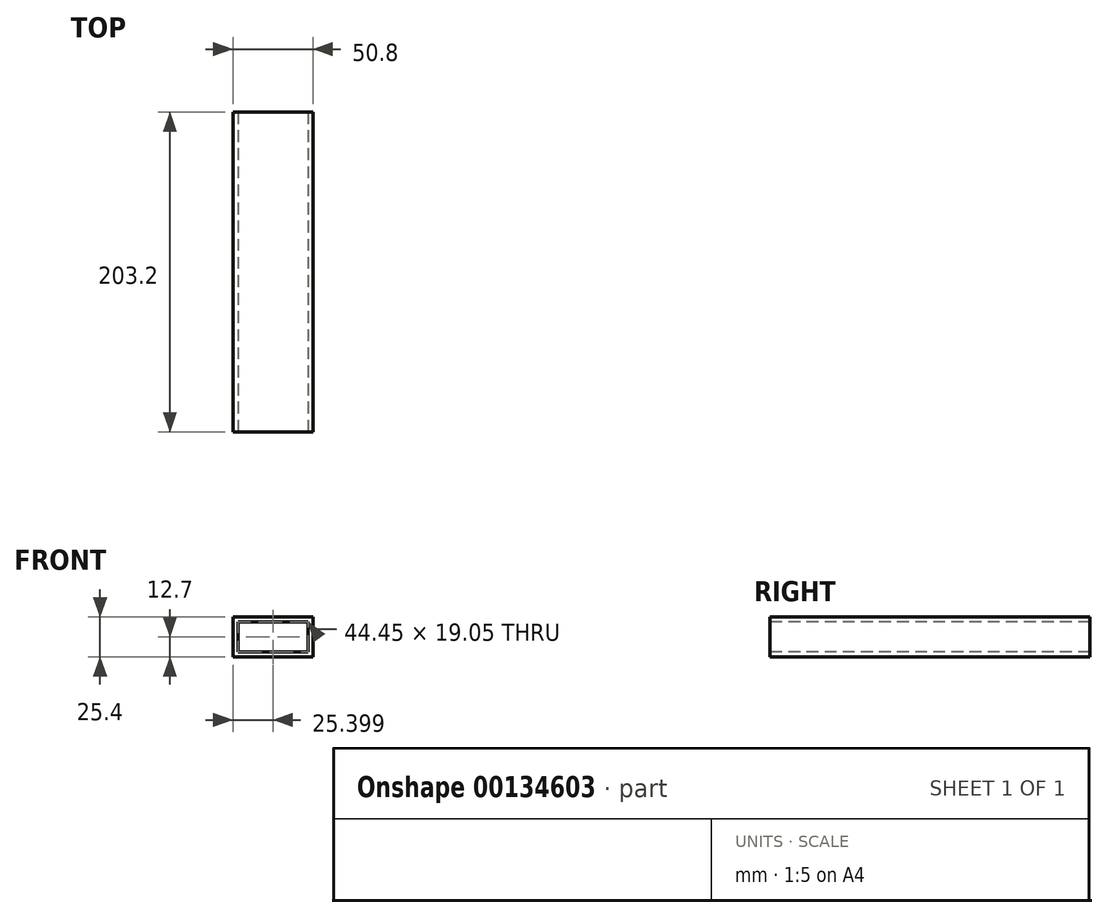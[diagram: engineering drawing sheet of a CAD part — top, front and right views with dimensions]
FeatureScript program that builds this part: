
annotation { "Feature Type Name" : "Feature", "Feature Type Description" : "" }
export const myFeature = defineFeature(function(context is Context, id is Id, definition is map)
    precondition{}
    {
        {
            var Q0;
            Q0=qCreatedBy(makeId("Top.planeOp"),FACE);
            var sketch = newSketch(context, id + "F0", { "sketchPlane" : qUnion([Q0])});
            skLineSegment(sketch, "E0.bottom", {"start": v(-36.05, 90.68) * mm, "end": v(14.75, 90.68) * mm});
            skLineSegment(sketch, "E0.top", {"start": v(-36.05, -112.52) * mm, "end": v(14.75, -112.52) * mm});
            skLineSegment(sketch, "E0.left", {"start": v(-36.05, 90.68) * mm, "end": v(-36.05, -112.52) * mm});
            skLineSegment(sketch, "E0.right", {"start": v(14.75, 90.68) * mm, "end": v(14.75, -112.52) * mm});
            skSolve(sketch);
        }
        {
            var Q0;
            Q0 = qSketchRegion(id + "F0", true);
            extrude(context, id + "F1", {"entities" : qUnion([Q0]), "endBound" : BoundingType.SYMMETRIC, "depth" : 25.4 * mm});
        }
        {
            var Q0;
            Q0=makeQuery(id+"F1.opExtrude","SWEPT_FACE",FACE,{"disambiguationData":[OSD([sQuery(id+"F0.wireOp",EDGE,"E0.top")])]});
            var Q1;
            Q1=makeQuery(id+"F1.opExtrude","SWEPT_FACE",FACE,{"disambiguationData":[OSD([sQuery(id+"F0.wireOp",EDGE,"E0.bottom")])]});
            var Q2;
            Q2=makeQuery(id+"F1.opExtrude","SWEPT_BODY",BODY,{"disambiguationData":[OSD([sQuery(id+"F0.wireOp",EDGE,"E0.bottom"),sQuery(id+"F0.wireOp",EDGE,"E0.top"),sQuery(id+"F0.wireOp",EDGE,"E0.left"),sQuery(id+"F0.wireOp",EDGE,"E0.right")])]});
            shell(context, id + "F2", {"entities" : qUnion([Q0, Q1]), "parts" : qUnion([Q2]), "thickness" : 3.17 * mm});
        }
    });
